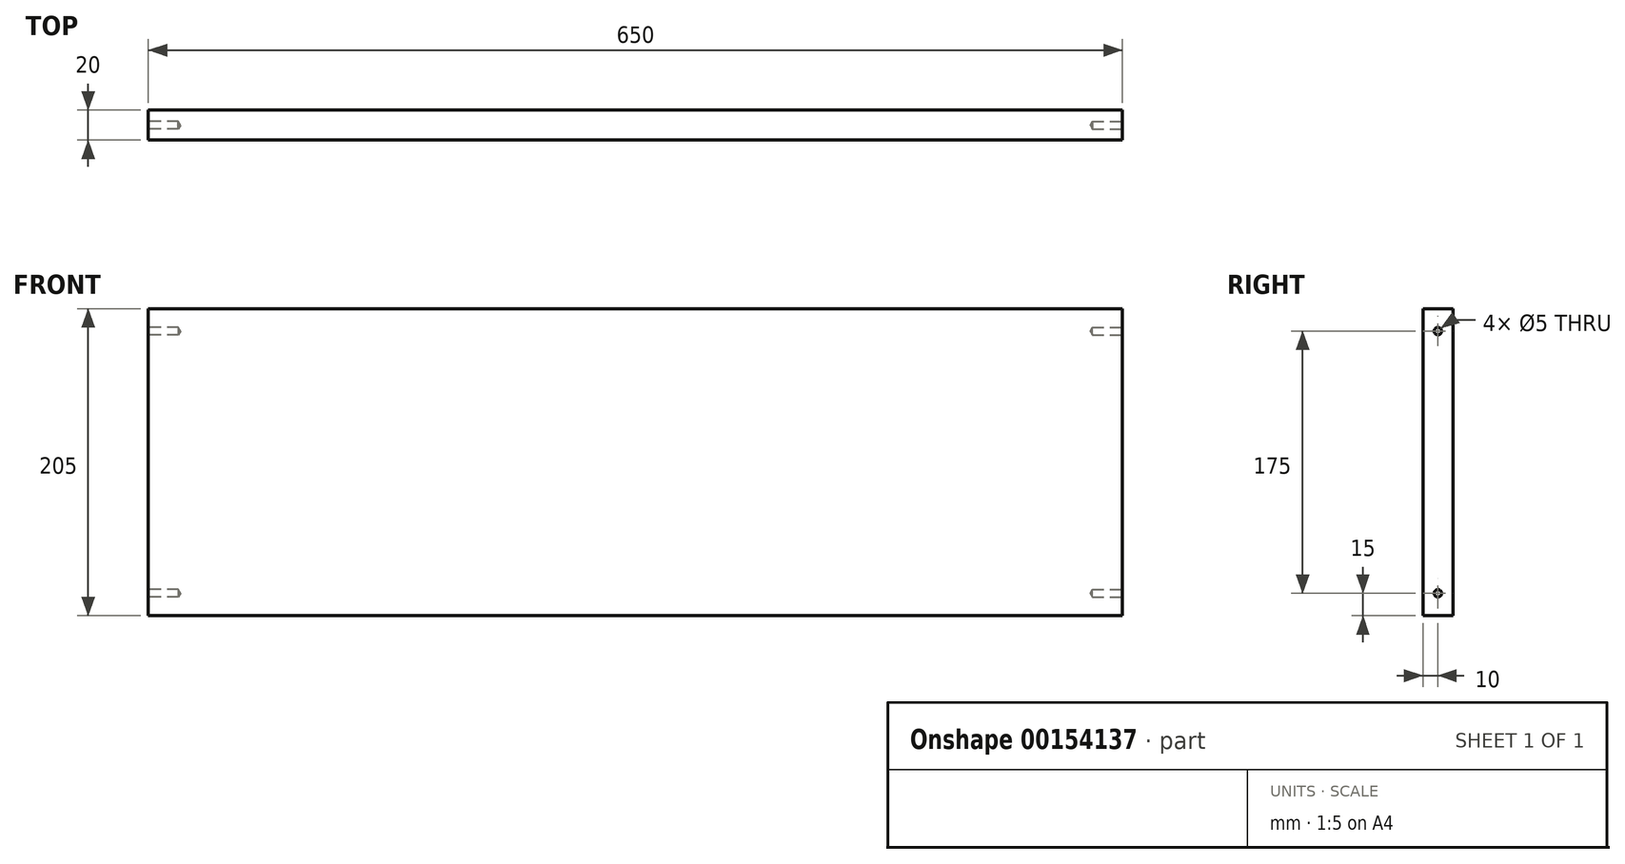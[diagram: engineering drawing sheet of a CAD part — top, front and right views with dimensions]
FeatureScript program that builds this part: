
annotation { "Feature Type Name" : "Feature", "Feature Type Description" : "" }
export const myFeature = defineFeature(function(context is Context, id is Id, definition is map)
    precondition{}
    {
        {
            var Q0;
            Q0=qCreatedBy(makeId("Front.planeOp"),FACE);
            var sketch = newSketch(context, id + "F0", { "sketchPlane" : qUnion([Q0])});
            skLineSegment(sketch, "E0.bottom", {"start": v(325, -102.5) * mm, "end": v(-325, -102.5) * mm});
            skLineSegment(sketch, "E0.top", {"start": v(325, 102.5) * mm, "end": v(-325, 102.5) * mm});
            skLineSegment(sketch, "E0.left", {"start": v(325, -102.5) * mm, "end": v(325, 102.5) * mm});
            skLineSegment(sketch, "E0.right", {"start": v(-325, -102.5) * mm, "end": v(-325, 102.5) * mm});
            skPoint(sketch, "E0.middle", {"position": v(0, 0) * mm});
            skSolve(sketch);
        }
        {
            var Q0;
            Q0 = qSketchRegion(id + "F0", true);
            extrude(context, id + "F1", {"entities" : qUnion([Q0]), "depth" : 20 * mm});
        }
        {
            var Q0;
            Q0=makeQuery(id+"F1.opExtrude","SWEPT_FACE",FACE,{"disambiguationData":[OSD([sQuery(id+"F0.wireOp",EDGE,"E0.left")])]});
            var sketch = newSketch(context, id + "F2", { "sketchPlane" : qUnion([Q0])});
            skPoint(sketch, "E1", {"position": v(-10, 87.5) * mm});
            skPoint(sketch, "E2", {"position": v(-10, -87.5) * mm});
            skSolve(sketch);
        }
        {
            var Q0;
            Q0=sQuery(id+"F2.wireOp",VERTEX,"E1");
            var Q1;
            Q1=sQuery(id+"F2.wireOp",VERTEX,"E2");
            var Q2;
            Q2=makeQuery(id+"F1.opExtrude","SWEPT_BODY",BODY,{"disambiguationData":[OSD([sQuery(id+"F0.wireOp",EDGE,"E0.bottom"),sQuery(id+"F0.wireOp",EDGE,"E0.top"),sQuery(id+"F0.wireOp",EDGE,"E0.left"),sQuery(id+"F0.wireOp",EDGE,"E0.right")])]});
            hole(context, id + "F3", {"style" : HoleStyle.SIMPLE, "endStyle" : HoleEndStyle.BLIND, "standardTappedOrClearance" : lookupTablePath({ "standard" : "ISO", "engagement" : "75%", "pitch" : "1 mm", "size" : "M6", "type" : "Tapped" }), "standardBlindInLast" : lookupTablePath({ "standard" : "ISO", "engagement" : "75%", "pitch" : "1 mm", "size" : "M6", "type" : "Tapped" }), "holeDiameter" : 5 * mm, "holeDepth" : 20 * mm, "locations" : qUnion([Q0, Q1]), "scope" : qUnion([Q2]), "majorDiameter" : 6 * mm});
        }
        {
            var Q0;
            Q0=makeQuery(id+"F1.opExtrude","SWEPT_FACE",FACE,{"disambiguationData":[OSD([sQuery(id+"F0.wireOp",EDGE,"E0.right")])]});
            var sketch = newSketch(context, id + "F4", { "sketchPlane" : qUnion([Q0])});
            skPoint(sketch, "E3", {"position": v(10, 87.5) * mm});
            skPoint(sketch, "E4", {"position": v(10, -87.5) * mm});
            skSolve(sketch);
        }
        {
            var Q0;
            Q0=sQuery(id+"F4.wireOp",VERTEX,"E3");
            var Q1;
            Q1=sQuery(id+"F4.wireOp",VERTEX,"E4");
            var Q2;
            Q2=makeQuery(id+"F1.opExtrude","SWEPT_BODY",BODY,{"disambiguationData":[OSD([sQuery(id+"F0.wireOp",EDGE,"E0.bottom"),sQuery(id+"F0.wireOp",EDGE,"E0.top"),sQuery(id+"F0.wireOp",EDGE,"E0.left"),sQuery(id+"F0.wireOp",EDGE,"E0.right")])]});
            hole(context, id + "F5", {"style" : HoleStyle.SIMPLE, "endStyle" : HoleEndStyle.BLIND, "standardTappedOrClearance" : lookupTablePath({ "standard" : "ISO", "engagement" : "75%", "pitch" : "1 mm", "size" : "M6", "type" : "Tapped" }), "standardBlindInLast" : lookupTablePath({ "standard" : "ISO", "engagement" : "75%", "pitch" : "1 mm", "size" : "M6", "type" : "Tapped" }), "holeDiameter" : 5 * mm, "holeDepth" : 20 * mm, "locations" : qUnion([Q0, Q1]), "scope" : qUnion([Q2]), "majorDiameter" : 6 * mm});
        }
    });
